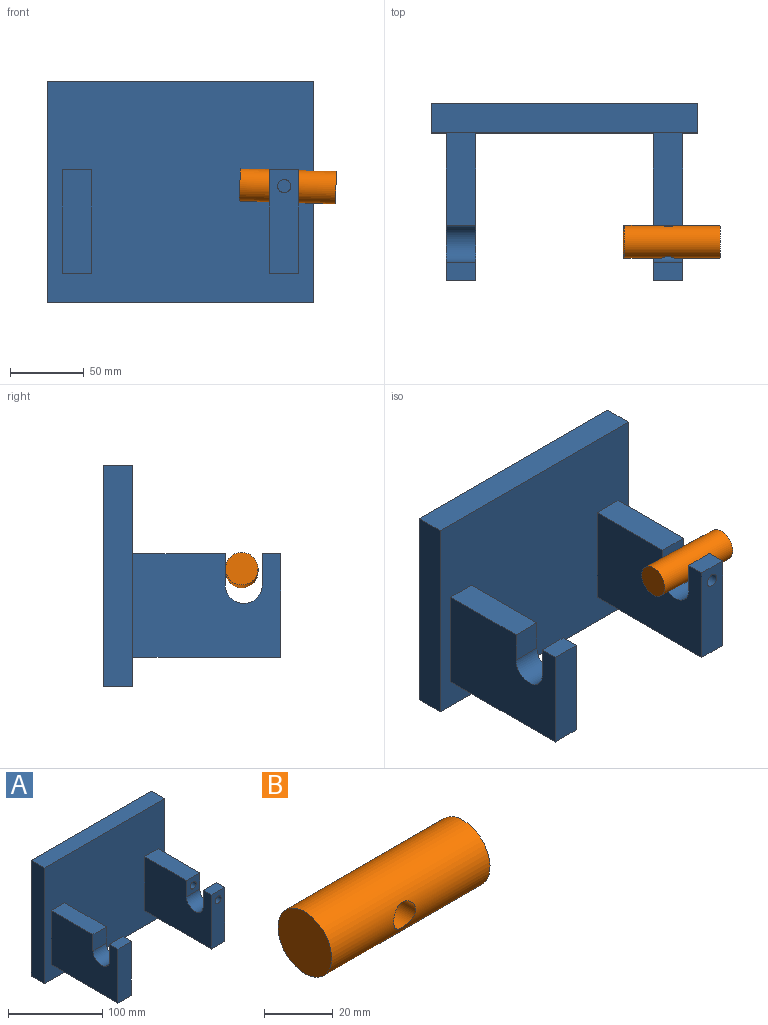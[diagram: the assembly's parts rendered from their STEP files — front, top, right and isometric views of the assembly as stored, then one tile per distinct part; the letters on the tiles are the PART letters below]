
ASSEMBLY  parts=2 mates=1
PART A: 27 faces, bbox 180x120x150 mm
  f0: plane 62.5x20mm, normal (0,0,1), area 1250mm2, adj f2,f3,f6,f22
  f1: plane 62.5x20mm, normal (0,0,1), area 1250mm2, adj f4,f5,f6,f19
  f2: plane 100x70mm, normal (-1,0,0), area 6229.6mm2, adj f0,f6,f12,f13,f14,f21,f22,f23
  f3: plane 100x70mm, normal (1,0,0), area 6229.6mm2, adj f0,f6,f12,f13,f14,f21,f22,f23
  f4: plane 100x70mm, normal (-1,0,0), area 6229.6mm2, adj f1,f6,f15,f16,f17,f18,f19,f20
  f5: plane 100x70mm, normal (1,0,0), area 6229.6mm2, adj f1,f6,f15,f16,f17,f18,f19,f20
  f6: plane 180x150mm, normal (0,-1,0), area 24200mm2, adj f0,f1,f2,f3,f4,f5,f7,f8
  f7: plane 150x20mm, normal (-1,0,0), area 3000mm2, adj f6,f8,f10,f11
  f8: plane 180x20mm, normal (0,0,-1), area 3600mm2, adj f6,f7,f9,f11
  f9: plane 150x20mm, normal (1,0,0), area 3000mm2, adj f6,f8,f10,f11
  f10: plane 180x20mm, normal (0,0,1), area 3600mm2, adj f6,f7,f9,f11
  f11: plane 180x150mm, normal (0,1,0), area 27000mm2, adj f7,f8,f9,f10
  f12: plane 20x12.5mm, normal (0,0,1), area 250mm2, adj f2,f3,f14,f21
  f13: plane 100x20mm, normal (0,0,-1), area 2000mm2, adj f2,f3,f6,f14
  f14: plane 70x20mm, normal (0,-1,0), area 1400mm2, adj f2,f3,f12,f13
  f15: plane 20x12.5mm, normal (0,0,1), area 250mm2, adj f4,f5,f17,f20
  f16: plane 100x20mm, normal (0,0,-1), area 2000mm2, adj f4,f5,f6,f17
  f17: plane 70x20mm, normal (0,-1,0), area 1336.4mm2, adj f4,f5,f15,f16,f24
  f18: cylinder r=12.5mm len=25mm, axis (1,0,0), area 785.4mm2, adj f4,f5,f19,f20
  f19: plane 21x20mm, normal (0,-1,0), area 356.4mm2, adj f1,f4,f5,f18,f25
  f20: plane 21x20mm, normal (0,1,0), area 356.4mm2, adj f4,f5,f15,f18,f24
  f21: plane 21x20mm, normal (0,1,0), area 420mm2, adj f2,f3,f12,f23
  f22: plane 21x20mm, normal (0,-1,0), area 420mm2, adj f0,f2,f3,f23
  f23: cylinder r=12.5mm len=25mm, axis (1,0,0), area 785.4mm2, adj f2,f3,f21,f22
  f24: cylinder r=4.5mm len=12.5mm, axis (0,-1,0), area 353.4mm2, adj f17,f20
  f25: cylinder r=4.5mm len=12.5mm, axis (0,-1,0), area 353.4mm2, adj f19,f26
  f26: plane 9x9mm, normal (0,-1,0), area 63.6mm2, adj f25
PART B: 4 faces, bbox 65x22x22 mm
  f0: cylinder r=11mm len=65mm, axis (-1,0,0), area 4362.4mm2, adj f1,f2,f3
  f1: plane 22x22mm, normal (1,0,0), area 380.1mm2, adj f0
  f2: plane 22x22mm, normal (-1,0,0), area 380.1mm2, adj f0
  f3: cylinder r=4.5mm len=22mm, axis (0,-1,0), area 595.1mm2, adj f0
PLACE A t=(-53.79,-8.88,-5.71)mm fixed
PLACE B rot(axis=(0,1,0),1.7deg) t=(76.23,-102.52,74.2)mm
MATE revolute A.f24 <-> B.f3  axis (0,-1,0) through (106.21,-91.38,73.29)mm
